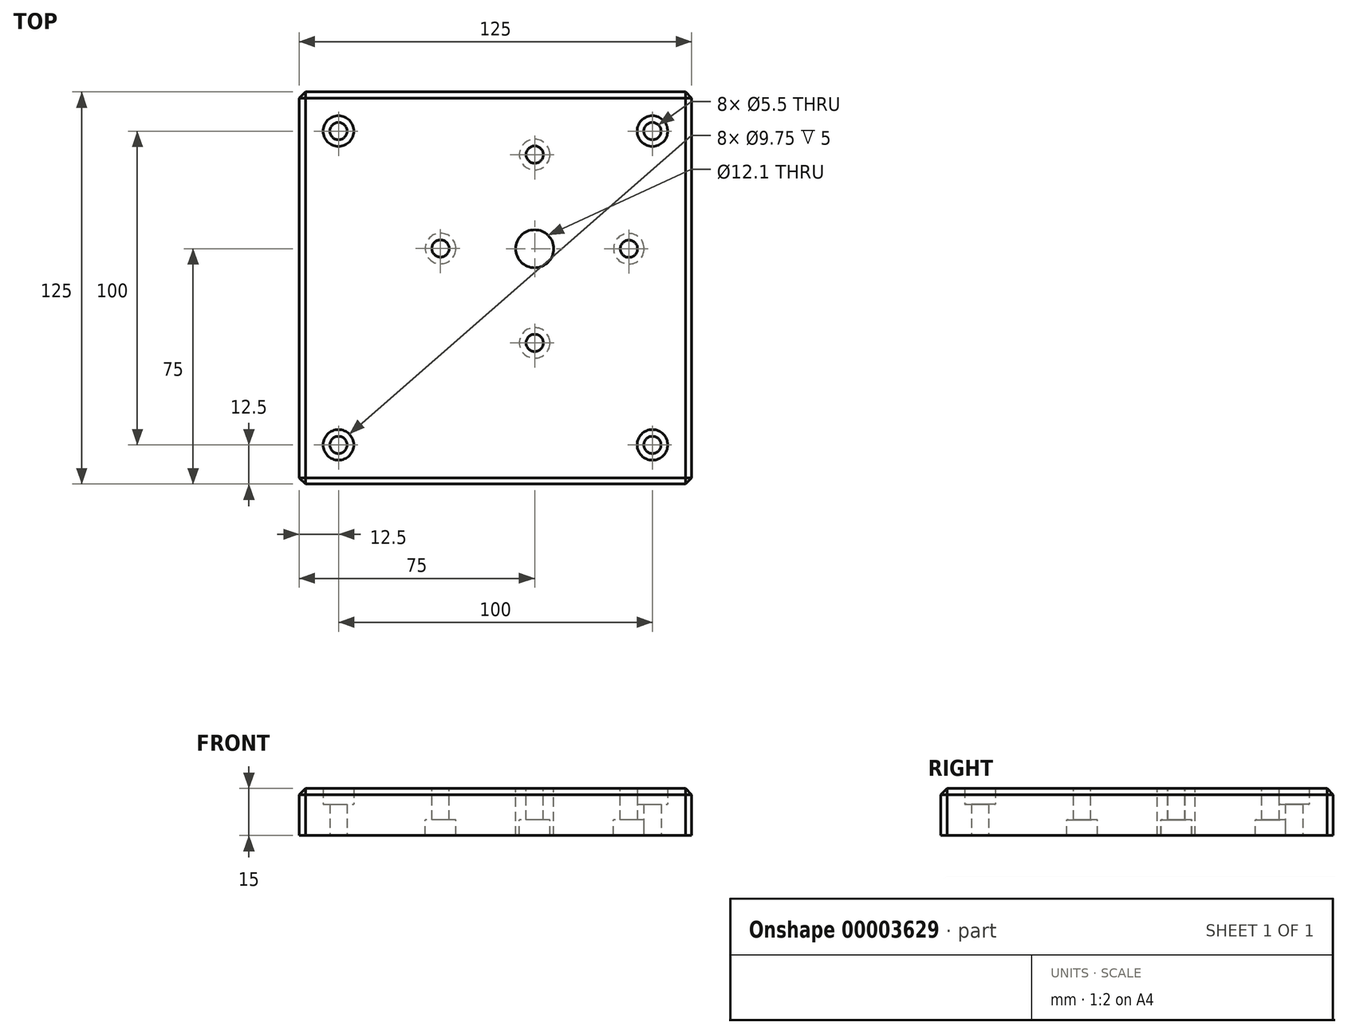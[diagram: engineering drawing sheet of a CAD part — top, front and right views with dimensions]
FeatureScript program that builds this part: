
annotation { "Feature Type Name" : "Feature", "Feature Type Description" : "" }
export const myFeature = defineFeature(function(context is Context, id is Id, definition is map)
    precondition{}
    {
        {
            var Q0;
            Q0=qCreatedBy(makeId("Top.planeOp"),FACE);
            var sketch = newSketch(context, id + "F0", { "sketchPlane" : qUnion([Q0])});
            skLineSegment(sketch, "E0.bottom", {"start": v(0, 0) * mm, "end": v(-125, 0) * mm});
            skLineSegment(sketch, "E0.top", {"start": v(0, 125) * mm, "end": v(-125, 125) * mm});
            skLineSegment(sketch, "E0.left", {"start": v(0, 0) * mm, "end": v(0, 125) * mm});
            skLineSegment(sketch, "E0.right", {"start": v(-125, 0) * mm, "end": v(-125, 125) * mm});
            skSolve(sketch);
        }
        {
            var Q0;
            Q0=makeQuery(id+"F0.imprint","IMPRINT",FACE,{"disambiguationData":[TD([[makeQuery(id+"F0.imprint","IMPRINT",EDGE,{"derivedFrom":sQuery(id+"F0.wireOp",EDGE,"E0.bottom")}),-1.0]])]});
            extrude(context, id + "F1", {"entities" : qUnion([Q0]), "depth" : 15 * mm});
        }
        {
            var Q0;
            Q0=makeQuery(id+"F1.opExtrude","CAP_EDGE",EDGE,{"disambiguationData":[OSD([sQuery(id+"F0.wireOp",EDGE,"E0.bottom")])],"isStart":false});
            var Q1;
            Q1=makeQuery(id+"F1.opExtrude","CAP_EDGE",EDGE,{"disambiguationData":[OSD([sQuery(id+"F0.wireOp",EDGE,"E0.left")])],"isStart":false});
            var Q2;
            Q2=makeQuery(id+"F1.opExtrude","CAP_EDGE",EDGE,{"disambiguationData":[OSD([sQuery(id+"F0.wireOp",EDGE,"E0.top")])],"isStart":false});
            var Q3;
            Q3=makeQuery(id+"F1.opExtrude","CAP_EDGE",EDGE,{"disambiguationData":[OSD([sQuery(id+"F0.wireOp",EDGE,"E0.right")])],"isStart":false});
            var Q4;
            Q4=makeQuery(id+"F1.opExtrude","SWEPT_EDGE",EDGE,{"disambiguationData":[OSD([sQuery(id+"F0.wireOp",EDGE,"E0.bottom"),sQuery(id+"F0.wireOp",EDGE,"E0.left")])]});
            var Q5;
            Q5=makeQuery(id+"F1.opExtrude","SWEPT_EDGE",EDGE,{"disambiguationData":[OSD([sQuery(id+"F0.wireOp",EDGE,"E0.top"),sQuery(id+"F0.wireOp",EDGE,"E0.left")])]});
            var Q6;
            Q6=makeQuery(id+"F1.opExtrude","SWEPT_EDGE",EDGE,{"disambiguationData":[OSD([sQuery(id+"F0.wireOp",EDGE,"E0.top"),sQuery(id+"F0.wireOp",EDGE,"E0.right")])]});
            var Q7;
            Q7=makeQuery(id+"F1.opExtrude","SWEPT_EDGE",EDGE,{"disambiguationData":[OSD([sQuery(id+"F0.wireOp",EDGE,"E0.bottom"),sQuery(id+"F0.wireOp",EDGE,"E0.right")])]});
            chamfer(context, id + "F2", {"entities" : qUnion([Q0, Q1, Q2, Q3, Q4, Q5, Q6, Q7]), "width" : 2 * mm, "tangentPropagation" : true});
        }
        {
            var Q0;
            Q0=makeQuery(id+"F1.opExtrude","CAP_FACE",FACE,{"disambiguationData":[OSD([sQuery(id+"F0.wireOp",EDGE,"E0.bottom"),sQuery(id+"F0.wireOp",EDGE,"E0.top"),sQuery(id+"F0.wireOp",EDGE,"E0.left"),sQuery(id+"F0.wireOp",EDGE,"E0.right")])],"isStart":true});
            var sketch = newSketch(context, id + "F3", { "sketchPlane" : qUnion([Q0])});
            skPoint(sketch, "E1", {"position": v(-50, -105) * mm});
            skPoint(sketch, "E2", {"position": v(-20, -75) * mm});
            skPoint(sketch, "E3", {"position": v(-50, -45) * mm});
            skPoint(sketch, "E4", {"position": v(-50, -75) * mm});
            skPoint(sketch, "E5", {"position": v(-80, -75.08) * mm});
            skCircle(sketch, "E6", {"center": v(-50, -75) * mm, "radius": 30 * mm, "construction": true});
            skSolve(sketch);
        }
        {
            var Q0;
            Q0=sQuery(id+"F3.wireOp",VERTEX,"E5");
            var Q1;
            Q1=sQuery(id+"F3.wireOp",VERTEX,"E1");
            var Q2;
            Q2=sQuery(id+"F3.wireOp",VERTEX,"E2");
            var Q3;
            Q3=sQuery(id+"F3.wireOp",VERTEX,"E3");
            var Q4;
            Q4=makeQuery(id+"F1.opExtrude","SWEPT_BODY",BODY,{"disambiguationData":[OSD([sQuery(id+"F0.wireOp",EDGE,"E0.bottom"),sQuery(id+"F0.wireOp",EDGE,"E0.top"),sQuery(id+"F0.wireOp",EDGE,"E0.left"),sQuery(id+"F0.wireOp",EDGE,"E0.right")])]});
            hole(context, id + "F4", {"style" : HoleStyle.C_BORE, "endStyle" : HoleEndStyle.THROUGH, "standardTappedOrClearance" : lookupTablePath({ "standard" : "ISO", "fit" : "Normal", "size" : "M5", "type" : "Clearance" }), "standardBlindInLast" : lookupTablePath({ "fit" : "Standard", "standard" : "ISO", "size" : "M5", "type" : "Clearance" }), "holeDiameter" : 5.5 * mm, "cBoreDiameter" : 9.75 * mm, "cBoreDepth" : 5 * mm, "tappedDepth" : 2 * mm, "tapClearance" : 3, "locations" : qUnion([Q0, Q1, Q2, Q3]), "scope" : qUnion([Q4]), "startStyle" : HoleStartStyle.SKETCH});
        }
        {
            var Q0;
            Q0=sQuery(id+"F3.wireOp",VERTEX,"E4");
            var Q1;
            Q1=makeQuery(id+"F1.opExtrude","SWEPT_BODY",BODY,{"disambiguationData":[OSD([sQuery(id+"F0.wireOp",EDGE,"E0.bottom"),sQuery(id+"F0.wireOp",EDGE,"E0.top"),sQuery(id+"F0.wireOp",EDGE,"E0.left"),sQuery(id+"F0.wireOp",EDGE,"E0.right")])]});
            hole(context, id + "F5", {"style" : HoleStyle.SIMPLE, "endStyle" : HoleEndStyle.THROUGH, "standardTappedOrClearance" : lookupTablePath({ "standard" : "ISO", "engagement" : "75%", "pitch" : "2 mm", "size" : "M14", "type" : "Tapped" }), "standardBlindInLast" : lookupTablePath({ "standard" : "ISO", "engagement" : "75%", "pitch" : "2 mm", "size" : "M14", "type" : "Tapped" }), "holeDiameter" : 12.1 * mm, "showTappedDepth" : true, "tappedDepth" : 2 * mm, "tapClearance" : 3, "locations" : qUnion([Q0]), "scope" : qUnion([Q1]), "majorDiameter" : 14 * mm, "startStyle" : HoleStartStyle.SKETCH});
        }
        {
            var Q0;
            Q0=makeQuery(id+"F1.opExtrude","CAP_FACE",FACE,{"disambiguationData":[OSD([sQuery(id+"F0.wireOp",EDGE,"E0.bottom"),sQuery(id+"F0.wireOp",EDGE,"E0.top"),sQuery(id+"F0.wireOp",EDGE,"E0.left"),sQuery(id+"F0.wireOp",EDGE,"E0.right")])],"isStart":false});
            var sketch = newSketch(context, id + "F6", { "sketchPlane" : qUnion([Q0])});
            skPoint(sketch, "E7", {"position": v(-112.5, 112.5) * mm});
            skPoint(sketch, "E8", {"position": v(-12.5, 112.5) * mm});
            skPoint(sketch, "E9", {"position": v(-12.5, 12.5) * mm});
            skPoint(sketch, "E10", {"position": v(-112.5, 12.5) * mm});
            skSolve(sketch);
        }
        {
            var Q0;
            Q0=sQuery(id+"F6.wireOp",VERTEX,"E7");
            var Q1;
            Q1=sQuery(id+"F6.wireOp",VERTEX,"E8");
            var Q2;
            Q2=sQuery(id+"F6.wireOp",VERTEX,"E9");
            var Q3;
            Q3=sQuery(id+"F6.wireOp",VERTEX,"E10");
            var Q4;
            Q4=makeQuery(id+"F1.opExtrude","SWEPT_BODY",BODY,{"disambiguationData":[OSD([sQuery(id+"F0.wireOp",EDGE,"E0.bottom"),sQuery(id+"F0.wireOp",EDGE,"E0.top"),sQuery(id+"F0.wireOp",EDGE,"E0.left"),sQuery(id+"F0.wireOp",EDGE,"E0.right")])]});
            hole(context, id + "F7", {"style" : HoleStyle.C_BORE, "endStyle" : HoleEndStyle.THROUGH, "standardTappedOrClearance" : lookupTablePath({ "standard" : "ISO", "fit" : "Normal", "size" : "M5", "type" : "Clearance" }), "standardBlindInLast" : lookupTablePath({ "fit" : "Standard", "standard" : "ISO", "size" : "M5", "type" : "Clearance" }), "holeDiameter" : 5.5 * mm, "cBoreDiameter" : 9.75 * mm, "cBoreDepth" : 5 * mm, "tappedDepth" : 2 * mm, "tapClearance" : 3, "locations" : qUnion([Q0, Q1, Q2, Q3]), "scope" : qUnion([Q4]), "startStyle" : HoleStartStyle.SKETCH});
        }
    });
